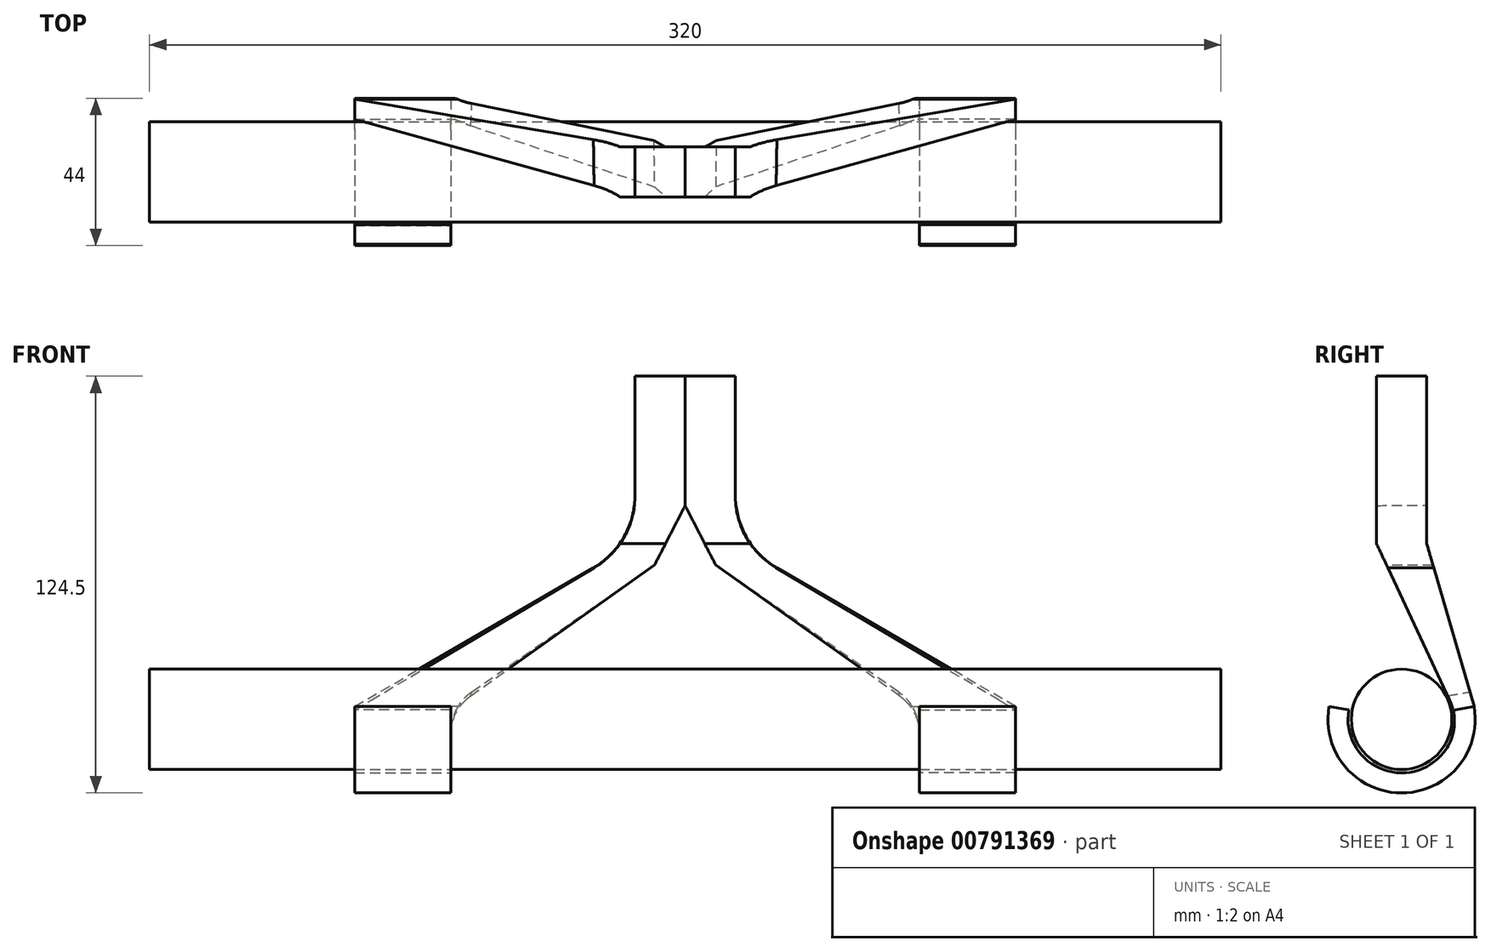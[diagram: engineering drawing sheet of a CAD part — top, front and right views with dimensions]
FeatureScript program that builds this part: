
annotation { "Feature Type Name" : "Feature", "Feature Type Description" : "" }
export const myFeature = defineFeature(function(context is Context, id is Id, definition is map)
    precondition{}
    {
        {
            var Q0;
            Q0=qCreatedBy(makeId("Front.planeOp"),FACE);
            var sketch = newSketch(context, id + "F0", { "sketchPlane" : qUnion([Q0])});
            skLineSegment(sketch, "E0.bottom", {"start": v(60, -7.5) * mm, "end": v(-60, -7.5) * mm});
            skLineSegment(sketch, "E0.top", {"start": v(60, 7.5) * mm, "end": v(-60, 7.5) * mm});
            skLineSegment(sketch, "E0.left", {"start": v(60, -7.5) * mm, "end": v(60, 7.5) * mm, "construction": true});
            skLineSegment(sketch, "E0.right", {"start": v(-60, -7.5) * mm, "end": v(-60, 7.5) * mm, "construction": true});
            skPoint(sketch, "E0.middle", {"position": v(0, 0) * mm});
            skLineSegment(sketch, "E1", {"start": v(0, 7.5) * mm, "end": v(0, -7.5) * mm});
            skLineSegment(sketch, "E2.bottom", {"start": v(60, 7.5) * mm, "end": v(160, 7.5) * mm});
            skLineSegment(sketch, "E2.top", {"start": v(60, -7.5) * mm, "end": v(160, -7.5) * mm});
            skLineSegment(sketch, "E2.left", {"start": v(60, 7.5) * mm, "end": v(60, -7.5) * mm});
            skLineSegment(sketch, "E2.right", {"start": v(160, 7.5) * mm, "end": v(160, -7.5) * mm});
            skLineSegment(sketch, "E3.MirrorCS", {"start": v(-60, 7.5) * mm, "end": v(-160, 7.5) * mm});
            skLineSegment(sketch, "E4.MirrorCS", {"start": v(-60, -7.5) * mm, "end": v(-160, -7.5) * mm});
            skLineSegment(sketch, "E5.MirrorCS", {"start": v(-160, 7.5) * mm, "end": v(-160, -7.5) * mm});
            skSolve(sketch);
        }
        {
            var Q0;
            {var subQ1=sQuery(id+"F0.wireOp",EDGE,"E1");Q0=makeQuery(id+"F0.imprint","IMPRINT",FACE,{"disambiguationData":[TD([[makeQuery(id+"F0.imprint","IMPRINT",EDGE,{"derivedFrom":subQ1}),-1.0]])]});}
            var Q1;
            {var subQ2=sQuery(id+"F0.wireOp",EDGE,"E1");Q1=makeQuery(id+"F0.imprint","IMPRINT",FACE,{"disambiguationData":[TD([[makeQuery(id+"F0.imprint","IMPRINT",EDGE,{"derivedFrom":subQ2}),1.0]])]});}
            var Q2;
            Q2=makeQuery(id+"F0.imprint","IMPRINT",FACE,{"disambiguationData":[TD([[makeQuery(id+"F0.imprint","IMPRINT",EDGE,{"derivedFrom":sQuery(id+"F0.wireOp",EDGE,"E2.bottom")}),-1.0]])]});
            var Q3;
            Q3=sQuery(id+"F0.wireOp",EDGE,"E3.MirrorCS");
            revolve(context, id + "F1", {"surfaceOperationType" : NewSurfaceOperationType.NEW, "entities" : qUnion([Q0, Q1, Q2]), "axis" : qUnion([Q3]), "revolveType" : RevolveType.FULL});
        }
        {
            var Q0;
            Q0=qCreatedBy(makeId("Front.planeOp"),FACE);
            var sketch = newSketch(context, id + "F2", { "sketchPlane" : qUnion([Q0])});
            skLineSegment(sketch, "E6.bottom", {"start": v(70, -8.5) * mm, "end": v(98.72, -8.5) * mm});
            skLineSegment(sketch, "E6.top", {"start": v(70, -14.5) * mm, "end": v(98.72, -14.5) * mm});
            skLineSegment(sketch, "E6.left", {"start": v(70, -8.5) * mm, "end": v(70, -14.5) * mm});
            skLineSegment(sketch, "E6.right", {"start": v(98.72, -8.5) * mm, "end": v(98.72, -14.5) * mm});
            skSolve(sketch);
        }
        {
            var Q0;
            Q0=makeQuery(id+"F2.imprint","IMPRINT",FACE,{"disambiguationData":[TD([[makeQuery(id+"F2.imprint","IMPRINT",EDGE,{"derivedFrom":sQuery(id+"F2.wireOp",EDGE,"E6.bottom")}),-1.0]])]});
            var Q1;
            Q1=sQuery(id+"F0.wireOp",EDGE,"E2.bottom");
            revolve(context, id + "F3", {"surfaceOperationType" : NewSurfaceOperationType.NEW, "entities" : qUnion([Q0]), "axis" : qUnion([Q1]), "revolveType" : RevolveType.TWO_DIRECTIONS, "angle" : 100 * degree, "angleBack" : 260 * degree});
        }
        {
            var Q0;
            Q0=qCreatedBy(makeId("Top.planeOp"),FACE);
            cPlane(context, id + "F4", {"entities" : qUnion([Q0]), "cplaneType" : CPlaneType.OFFSET, "offset" : 60 * mm, "width" : 150 * mm, "height" : 150 * mm});
        }
        {
            var Q0;
            Q0=qCreatedBy(id+"F4.planeOp",FACE);
            var sketch = newSketch(context, id + "F5", { "sketchPlane" : qUnion([Q0])});
            skLineSegment(sketch, "E7.bottom", {"start": v(15, 7.5) * mm, "end": v(-15, 7.5) * mm});
            skLineSegment(sketch, "E7.top", {"start": v(15, -7.5) * mm, "end": v(-15, -7.5) * mm});
            skLineSegment(sketch, "E7.left", {"start": v(15, 7.5) * mm, "end": v(15, -7.5) * mm});
            skLineSegment(sketch, "E7.right", {"start": v(-15, 7.5) * mm, "end": v(-15, -7.5) * mm});
            skPoint(sketch, "E7.middle", {"position": v(0, 0) * mm});
            skLineSegment(sketch, "E8", {"start": v(0, 7.5) * mm, "end": v(0, -7.5) * mm});
            skSolve(sketch);
        }
        {
            var Q0;
            {var subQ0=sQuery(id+"F5.wireOp",EDGE,"E7.left");Q0=makeQuery(id+"F5.imprint","IMPRINT",FACE,{"disambiguationData":[TD([[makeQuery(id+"F5.imprint","IMPRINT",EDGE,{"derivedFrom":subQ0}),-1.0]])]});}
            extrude(context, id + "F6", {"entities" : qUnion([Q0]), "depth" : 50 * mm, "offsetDistance" : 25 * mm});
        }
        {
            var Q0;
            Q0=makeQuery(id+"F3.opRevolve","CAP_FACE",FACE,{"disambiguationData":[OSD([sQuery(id+"F2.wireOp",EDGE,"E6.bottom"),sQuery(id+"F2.wireOp",EDGE,"E6.top"),sQuery(id+"F2.wireOp",EDGE,"E6.left"),sQuery(id+"F2.wireOp",EDGE,"E6.right")])],"isStart":false});
            var Q1;
            Q1=makeQuery(id+"F6.opExtrude","CAP_FACE",FACE,{"disambiguationData":[OSD([sQuery(id+"F5.wireOp",EDGE,"E7.bottom"),sQuery(id+"F5.wireOp",EDGE,"E7.top"),sQuery(id+"F5.wireOp",EDGE,"E7.left"),sQuery(id+"F5.wireOp",EDGE,"E8")])],"isStart":true});
            loft(context, id + "F7", {"operationType" : NewBodyOperationType.ADD, "sheetProfilesArray" : [{ "sheetProfileEntities" : qUnion([Q0]) }, { "sheetProfileEntities" : qUnion([Q1]) }]});
        }
        {
            var Q0;
            Q0=makeQuery(id+"F3.opRevolve","SWEPT_BODY",BODY,{"disambiguationData":[OSD([sQuery(id+"F2.wireOp",EDGE,"E6.bottom"),sQuery(id+"F2.wireOp",EDGE,"E6.top"),sQuery(id+"F2.wireOp",EDGE,"E6.left"),sQuery(id+"F2.wireOp",EDGE,"E6.right")])]});
            var Q1;
            Q1=qCreatedBy(makeId("Right.planeOp"),FACE);
            mirror(context, id + "F8", {"operationType" : NewBodyOperationType.ADD, "entities" : qUnion([Q0]), "mirrorPlane" : qUnion([Q1])});
        }
        {
            var Q0;
            {var subQ0=sQuery(id+"F5.wireOp",EDGE,"E8");var subQ1=makeQuery(id+"F7.boolean.opBoolean","MERGE",EDGE,{"derivedFrom":[makeQuery(id+"F6.opExtrude","CAP_EDGE",EDGE,{"disambiguationData":[OSD([subQ0])],"isStart":true}),makeQuery(id+"F7.opLoft","MID_CAP_EDGE",EDGE,{"disambiguationData":[OSD([sQuery(id+"F5.wireOp",EDGE,"E7.bottom"),sQuery(id+"F5.wireOp",EDGE,"E7.top"),subQ0])],"capPos":1.0})]});Q0=makeQuery(id+"F8.boolean.opBoolean","MERGE",EDGE,{"derivedFrom":[subQ1,makeQuery(id+"F8.opPattern","COPY",EDGE,{"derivedFrom":subQ1,"instanceName":"1"})]});}
            chamfer(context, id + "F9", {"entities" : qUnion([Q0]), "width" : 22 * mm, "tangentPropagation" : true});
        }
        {
            var Q0;
            {var subQ0=sQuery(id+"F5.wireOp",EDGE,"E7.left");Q0=makeQuery(id+"F7.boolean.opBoolean","MERGE",EDGE,{"derivedFrom":[makeQuery(id+"F6.opExtrude","CAP_EDGE",EDGE,{"disambiguationData":[OSD([subQ0])],"isStart":true}),makeQuery(id+"F7.opLoft","MID_CAP_EDGE",EDGE,{"disambiguationData":[OSD([sQuery(id+"F5.wireOp",EDGE,"E7.bottom"),sQuery(id+"F5.wireOp",EDGE,"E7.top"),subQ0])],"capPos":1.0})]});}
            var Q1;
            {var subQ0=sQuery(id+"F5.wireOp",EDGE,"E7.left");Q1=makeQuery(id+"F8.opPattern","COPY",EDGE,{"derivedFrom":makeQuery(id+"F7.boolean.opBoolean","MERGE",EDGE,{"derivedFrom":[makeQuery(id+"F6.opExtrude","CAP_EDGE",EDGE,{"disambiguationData":[OSD([subQ0])],"isStart":true}),makeQuery(id+"F7.opLoft","MID_CAP_EDGE",EDGE,{"disambiguationData":[OSD([sQuery(id+"F5.wireOp",EDGE,"E7.bottom"),sQuery(id+"F5.wireOp",EDGE,"E7.top"),subQ0])],"capPos":1.0})]}),"instanceName":"1"});}
            fillet(context, id + "F10", {"entities" : qUnion([Q0, Q1]), "radius" : 25 * mm, "tangentPropagation" : true, "allowEdgeOverflow" : false});
        }
        {
            var Q0;
            {var subQ0=sQuery(id+"F2.wireOp",EDGE,"E6.bottom");Q0=makeQuery(id+"F8.opPattern","COPY",EDGE,{"derivedFrom":makeQuery(id+"F7.boolean.opBoolean","MERGE",EDGE,{"derivedFrom":[makeQuery(id+"F3.opRevolve","CAP_EDGE",EDGE,{"disambiguationData":[OSD([subQ0])],"isStart":false}),makeQuery(id+"F7.opLoft","MID_CAP_EDGE",EDGE,{"disambiguationData":[OSD([subQ0,sQuery(id+"F2.wireOp",EDGE,"E6.left"),sQuery(id+"F2.wireOp",EDGE,"E6.right")])],"capPos":0.0})]}),"instanceName":"1"});}
            var Q1;
            {var subQ0=sQuery(id+"F2.wireOp",EDGE,"E6.bottom");Q1=makeQuery(id+"F7.boolean.opBoolean","MERGE",EDGE,{"derivedFrom":[makeQuery(id+"F3.opRevolve","CAP_EDGE",EDGE,{"disambiguationData":[OSD([subQ0])],"isStart":false}),makeQuery(id+"F7.opLoft","MID_CAP_EDGE",EDGE,{"disambiguationData":[OSD([subQ0,sQuery(id+"F2.wireOp",EDGE,"E6.left"),sQuery(id+"F2.wireOp",EDGE,"E6.right")])],"capPos":0.0})]});}
            var Q2;
            {var subQ0=sQuery(id+"F2.wireOp",EDGE,"E6.left");Q2=makeQuery(id+"F7.boolean.opBoolean","MERGE",EDGE,{"derivedFrom":[makeQuery(id+"F3.opRevolve","CAP_EDGE",EDGE,{"disambiguationData":[OSD([subQ0])],"isStart":false}),makeQuery(id+"F7.opLoft","MID_CAP_EDGE",EDGE,{"disambiguationData":[OSD([sQuery(id+"F2.wireOp",EDGE,"E6.bottom"),sQuery(id+"F2.wireOp",EDGE,"E6.top"),subQ0])],"capPos":0.0})]});}
            var Q3;
            {var subQ0=sQuery(id+"F2.wireOp",EDGE,"E6.left");Q3=makeQuery(id+"F8.opPattern","COPY",EDGE,{"derivedFrom":makeQuery(id+"F7.boolean.opBoolean","MERGE",EDGE,{"derivedFrom":[makeQuery(id+"F3.opRevolve","CAP_EDGE",EDGE,{"disambiguationData":[OSD([subQ0])],"isStart":false}),makeQuery(id+"F7.opLoft","MID_CAP_EDGE",EDGE,{"disambiguationData":[OSD([sQuery(id+"F2.wireOp",EDGE,"E6.bottom"),sQuery(id+"F2.wireOp",EDGE,"E6.top"),subQ0])],"capPos":0.0})]}),"instanceName":"1"});}
            fillet(context, id + "F11", {"entities" : qUnion([Q0, Q1, Q2, Q3]), "radius" : 15 * mm, "tangentPropagation" : true, "allowEdgeOverflow" : false});
        }
    });
